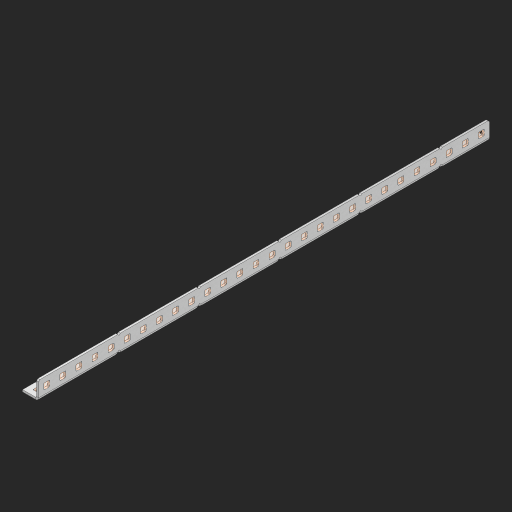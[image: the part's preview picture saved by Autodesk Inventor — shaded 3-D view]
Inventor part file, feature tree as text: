
AUTODESK INVENTOR PART (.ipt)
format: ipt  version: 2023 (Build 270158000, 158)  size: 1,191,936 bytes
history: native  units: in
note: dims shown in document units (in); Inventor stores cm internally (conversion verified against a paired STEP export)
features: other x232, extrude x82, sheet_metal_op x11, sketch x10, pattern_linear x2, mirror x1, chamfer x1
ambient origin geometry x8: Origin, YZ Plane, XZ Plane, XY Plane, X Axis, Y Axis, Z Axis, Center Point
bodies: Solid1 (feature_tree), Body (feature_tree)
feature tree (339):
  other  "Alu Half C 1x2x1x28"
  other  "Table"
  other  "Alu C 1x2x1x35"
  other  "Alu C 1x2x1x34"
  other  "Alu C 1x2x1x33"
  other  "Alu C 1x2x1x32"
  other  "Alu C 1x2x1x31"
  other  "Alu C 1x2x1x30"
  other  "Alu C 1x2x1x29"
  other  "Alu C 1x2x1x28"
  other  "Alu C 1x2x1x27"
  other  "Alu C 1x2x1x26"
  other  "Alu C 1x2x1x25"
  other  "Alu C 1x2x1x24"
  other  "Alu C 1x2x1x23"
  other  "Alu C 1x2x1x22"
  other  "Alu C 1x2x1x21"
  other  "Alu C 1x2x1x20"
  other  "Alu C 1x2x1x19"
  other  "Alu C 1x2x1x18"
  other  "Alu C 1x2x1x17"
  other  "Alu C 1x2x1x16"
  other  "Alu C 1x2x1x15"
  other  "Alu C 1x2x1x14"
  other  "Alu C 1x2x1x13"
  other  "Alu C 1x2x1x12"
  other  "Alu C 1x2x1x11"
  other  "Alu C 1x2x1x10"
  other  "Alu C 1x2x1x9"
  other  "Alu C 1x2x1x8"
  other  "Alu C 1x2x1x7"
  other  "Alu C 1x2x1x6"
  other  "Alu C 1x2x1x5"
  other  "Alu C 1x2x1x4"
  other  "Alu C 1x2x1x3"
  other  "Alu C 1x2x1x2"
  other  "Alu C 1x2x1x1"
  other  "Steel C 1x2x1x35"
  other  "Steel C 1x2x1x34"
  other  "Steel C 1x2x1x33"
  other  "Steel C 1x2x1x32"
  other  "Steel C 1x2x1x31"
  other  "Steel C 1x2x1x30"
  other  "Steel C 1x2x1x29"
  other  "Steel C 1x2x1x28"
  other  "Steel C 1x2x1x27"
  other  "Steel C 1x2x1x26"
  other  "Steel C 1x2x1x25"
  other  "Steel C 1x2x1x24"
  other  "Steel C 1x2x1x23"
  other  "Steel C 1x2x1x22"
  other  "Steel C 1x2x1x21"
  other  "Steel C 1x2x1x20"
  other  "Steel C 1x2x1x19"
  other  "Steel C 1x2x1x18"
  other  "Steel C 1x2x1x17"
  other  "Steel C 1x2x1x16"
  other  "Steel C 1x2x1x15"
  other  "Steel C 1x2x1x14"
  other  "Steel C 1x2x1x13"
  other  "Steel C 1x2x1x12"
  other  "Steel C 1x2x1x11"
  other  "Steel C 1x2x1x10"
  other  "Steel C 1x2x1x9"
  other  "Steel C 1x2x1x8"
  other  "Steel C 1x2x1x7"
  other  "Steel C 1x2x1x6"
  other  "Steel C 1x2x1x5"
  other  "Steel C 1x2x1x4"
  other  "Steel C 1x2x1x3"
  other  "Steel C 1x2x1x2"
  other  "Steel C 1x2x1x1"
  other  "Alu Half C 1x2x1x35"
  other  "Alu Half C 1x2x1x34"
  other  "Alu Half C 1x2x1x33"
  other  "Alu Half C 1x2x1x32"
  other  "Alu Half C 1x2x1x31"
  other  "Alu Half C 1x2x1x30"
  other  "Alu Half C 1x2x1x29"
  other  "Alu Half C 1x2x1x27"
  other  "Alu Half C 1x2x1x26"
  other  "Alu Half C 1x2x1x25"
  other  "Alu Half C 1x2x1x24"
  other  "Alu Half C 1x2x1x23"
  other  "Alu Half C 1x2x1x22"
  other  "Alu Half C 1x2x1x21"
  other  "Alu Half C 1x2x1x20"
  other  "Alu Half C 1x2x1x19"
  other  "Alu Half C 1x2x1x18"
  other  "Alu Half C 1x2x1x17"
  other  "Alu Half C 1x2x1x16"
  other  "Alu Half C 1x2x1x15"
  other  "Alu Half C 1x2x1x14"
  other  "Alu Half C 1x2x1x13"
  other  "Alu Half C 1x2x1x12"
  other  "Alu Half C 1x2x1x11"
  other  "Alu Half C 1x2x1x10"
  other  "Alu Half C 1x2x1x9"
  other  "Alu Half C 1x2x1x8"
  other  "Alu Half C 1x2x1x7"
  other  "Alu Half C 1x2x1x6"
  other  "Alu Half C 1x2x1x5"
  other  "Alu Half C 1x2x1x4"
  other  "Alu Half C 1x2x1x3"
  other  "Alu Half C 1x2x1x2"
  other  "Alu Half C 1x2x1x1"
  other  "Steel Half C 1x2x1x35"
  other  "Steel Half C 1x2x1x34"
  other  "Steel Half C 1x2x1x33"
  other  "Steel Half C 1x2x1x32"
  other  "Steel Half C 1x2x1x31"
  other  "Steel Half C 1x2x1x30"
  other  "Steel Half C 1x2x1x29"
  other  "Steel Half C 1x2x1x28"
  other  "Steel Half C 1x2x1x27"
  other  "Steel Half C 1x2x1x26"
  other  "Steel Half C 1x2x1x25"
  other  "Steel Half C 1x2x1x24"
  other  "Steel Half C 1x2x1x23"
  other  "Steel Half C 1x2x1x22"
  other  "Steel Half C 1x2x1x21"
  other  "Steel Half C 1x2x1x20"
  other  "Steel Half C 1x2x1x19"
  other  "Steel Half C 1x2x1x18"
  other  "Steel Half C 1x2x1x17"
  other  "Steel Half C 1x2x1x16"
  other  "Steel Half C 1x2x1x15"
  other  "Steel Half C 1x2x1x14"
  other  "Steel Half C 1x2x1x13"
  other  "Steel Half C 1x2x1x12"
  other  "Steel Half C 1x2x1x11"
  other  "Steel Half C 1x2x1x10"
  other  "Steel Half C 1x2x1x9"
  other  "Steel Half C 1x2x1x8"
  other  "Steel Half C 1x2x1x7"
  other  "Steel Half C 1x2x1x6"
  other  "Steel Half C 1x2x1x5"
  other  "Steel Half C 1x2x1x4"
  other  "Steel Half C 1x2x1x3"
  other  "Steel Half C 1x2x1x2"
  other  "Steel Half C 1x2x1x1"
  sheet_metal_op  "Flanges"
  other  "Flange Pattern Plane"
  other  "Flange Pattern Sketch"
  sheet_metal_op  "Flange Pattern"
  sheet_metal_op  "Body Pattern"
  pattern_linear  "Center Pattern"  Spacing1=0.0625in  [1 undecoded]
  other  "Arc Length"
  mirror  "Notch Mirror"
  pattern_linear  "Notch Pattern"  Spacing1=0.182in  [1 undecoded]
  chamfer  "End Chamfer"
  extrude  "Half Cut"  Depth=0.02in
  sketch  "Sketch1"  dims[d0=1.0in]
  other  "Plate1"
  sketch  "Sketch2"  dims[d1=14.0in]
  other  "Plate2"
  sheet_metal_op  "Bend1"
  sheet_metal_op  "Corner1"
  sketch  "Sketch3"  dims[d2=0.0625in]
  sketch  "Sketch7"  dims[d3=0.0625in]
  other  "Srf1"
  other  "Srf2"
  sketch  "Sketch8"  dims[d4=0.0312in]
  sketch  "Sketch9"  dims[d5=0.125in]
  other  "Srf91"
  sheet_metal_op  "Body Pattern Sketch"
  other  "Srf92"
  sketch  "Sketch13"  dims[d6=0.0625in]
  sketch  "Sketch14"  dims[d7=0.5in d8=90.0deg d9=0.0312in]
  sketch  "Sketch15"  dims[d10=0.25in]
  sketch  "Sketch16"  dims[d11=0.0625in d12=0.0625in d16=0.182in d17=0.02in d18=0.0625in d19=0.0in d20=0.25in d21=0.25in d38=11.0236in d40=0.5in d41=0.3937in d43=1.0in d46=0.172in d47=1.0in d48=0.0in d49=0.182in d50=0.02in d51=0.25in d52=0.25in d53=0.0625in d54=0.0in d55=0.172in d56=1.0in d57=0.0in d58=0.25in d60=11.0236in d62=0.5in d63=0.3937in d65=0.5in d85=0.1473in d86=0.1782in d88=0.04in d89=0.0625in d90=0.0in d91=0.04in d92=0.0491in d95=2.5in d96=0.04in d97=0.25in d98=45.0deg d99=0.25in d100=0.5in d101=0.0in d102=2.497in d106=0.182in d107=0.02in d108=0.5in d109=0.5in d110=0.0625in d111=0.0in d112=0.172in d113=0.5in d114=0.0in d117=0.5in d118=0.5in d119=0.5in]
  other  "Srf786"
  other  "Srf823"
  other  "Srf824"
  other  "Srf825"
  other  "Srf826"
  other  "Srf827"
  other  "Srf828"
  other  "Srf829"
  other  "Srf856"
  other  "Srf857"
  other  "Srf858"
  other  "Srf859"
  other  "Srf860"
  other  "Srf861"
  other  "Srf862"
  other  "Srf889"
  other  "Srf890"
  other  "Srf891"
  other  "Srf892"
  other  "Srf893"
  other  "Srf894"
  other  "Srf895"
  other  "Srf896"
  other  "Srf922"
  other  "Srf923"
  other  "Srf924"
  other  "Srf925"
  other  "Srf926"
  other  "Srf959"
  other  "Srf960"
  other  "Srf961"
  other  "Srf962"
  other  "Srf963"
  other  "Srf996"
  other  "Srf997"
  other  "Srf998"
  other  "Srf999"
  other  "Srf1000"
  other  "Srf1143"
  other  "Srf1144"
  other  "Srf1145"
  other  "Srf1146"
  other  "Srf1147"
  other  "Srf1148"
  other  "Srf1149"
  other  "Srf1150"
  other  "Srf1151"
  other  "Srf1152"
  other  "Srf1153"
  other  "Srf1154"
  other  "Srf1155"
  other  "Srf1156"
  other  "Srf1199"
  other  "Srf1200"
  other  "Srf1201"
  other  "Srf1202"
  other  "Srf1203"
  other  "Srf1204"
  other  "Srf1205"
  other  "Srf1206"
  other  "Srf1207"
  other  "Srf1208"
  other  "Srf1209"
  other  "Srf1210"
  other  "Srf1211"
  other  "Srf1212"
  other  "Srf1255"
  other  "Srf1256"
  other  "Srf1257"
  other  "Srf1258"
  other  "Srf1259"
  other  "Srf1260"
  other  "Srf1261"
  other  "Srf1262"
  other  "Srf1263"
  other  "Srf1264"
  other  "Srf1265"
  other  "Srf1266"
  other  "Srf1267"
  other  "Srf1268"
  sheet_metal_op  "Flange Stamp"
  sheet_metal_op  "Flange Circle"
  sheet_metal_op  "Body Stamp"
  sheet_metal_op  "Body Circle"
  other  "Center Stamp"
  other  "Center Circle"
  sheet_metal_op  "Notch"
  extrude  "ExtrusionSrf2"  Depth=0.0625in
  extrude  "ExtrusionSrf92"  TaperAngle=0.0deg  [1 undecoded]
  extrude  "ExtrusionSrf823"  Depth=0.25in
  extrude  "ExtrusionSrf824"  Depth=0.25in
  extrude  "ExtrusionSrf825"  Depth=0.5in
  extrude  "ExtrusionSrf826"  Depth=0.5in
  extrude  "ExtrusionSrf827"  Depth=1.0in TaperAngle=0.0deg
  extrude  "ExtrusionSrf828"  Depth=0.182in
  extrude  "ExtrusionSrf829"  Depth=0.02in
  extrude  "ExtrusionSrf856"  Depth=0.25in
  extrude  "ExtrusionSrf857"  Depth=0.25in
  extrude  "ExtrusionSrf858"  Depth=0.0625in
  extrude  "ExtrusionSrf859"  TaperAngle=0.0deg  [1 undecoded]
  extrude  "ExtrusionSrf860"  Depth=0.5in
  extrude  "ExtrusionSrf861"  Depth=1.0in TaperAngle=0.0deg
  extrude  "ExtrusionSrf862"  Depth=0.25in
  extrude  "ExtrusionSrf889"  Depth=0.5in
  extrude  "ExtrusionSrf890"  Depth=0.5in
  extrude  "ExtrusionSrf891"  Depth=0.5in
  extrude  "ExtrusionSrf892"  Depth=0.5in
  extrude  "ExtrusionSrf893"  Depth=0.5in
  extrude  "ExtrusionSrf894"  Depth=0.0625in
  extrude  "ExtrusionSrf895"  TaperAngle=0.0deg  [1 undecoded]
  extrude  "ExtrusionSrf896"  Depth=0.5in
  extrude  "ExtrusionSrf922"  Depth=0.5in
  extrude  "ExtrusionSrf923"  Depth=2.5in
  extrude  "ExtrusionSrf924"  Depth=0.25in TaperAngle=45.0deg
  extrude  "ExtrusionSrf925"  Depth=0.25in
  extrude  "ExtrusionSrf926"  Depth=0.5in TaperAngle=0.0deg
  extrude  "ExtrusionSrf959"  Depth=0.5in
  extrude  "ExtrusionSrf960"  Depth=0.182in
  extrude  "ExtrusionSrf961"  Depth=0.02in
  extrude  "ExtrusionSrf962"  Depth=0.5in
  extrude  "ExtrusionSrf963"  Depth=0.5in
  extrude  "ExtrusionSrf996"  Depth=0.0625in
  extrude  "ExtrusionSrf997"  TaperAngle=0.0deg  [1 undecoded]
  extrude  "ExtrusionSrf998"  Depth=0.5in
  extrude  "ExtrusionSrf999"  Depth=0.5in TaperAngle=0.0deg
  extrude  "ExtrusionSrf1000"  Depth=0.5in
  extrude  "ExtrusionSrf1143"  Depth=0.5in
  extrude  "ExtrusionSrf1144"  Depth=0.5in
  extrude  "ExtrusionSrf1145"  [1 undecoded]
  extrude  "ExtrusionSrf1146"  [1 undecoded]
  extrude  "ExtrusionSrf1147"  [1 undecoded]
  extrude  "ExtrusionSrf1148"  [1 undecoded]
  extrude  "ExtrusionSrf1149"  [1 undecoded]
  extrude  "ExtrusionSrf1150"  [1 undecoded]
  extrude  "ExtrusionSrf1151"  [1 undecoded]
  extrude  "ExtrusionSrf1152"  [1 undecoded]
  extrude  "ExtrusionSrf1153"  [1 undecoded]
  extrude  "ExtrusionSrf1154"  [1 undecoded]
  extrude  "ExtrusionSrf1155"  [1 undecoded]
  extrude  "ExtrusionSrf1156"  [1 undecoded]
  extrude  "ExtrusionSrf1199"  [1 undecoded]
  extrude  "ExtrusionSrf1200"  [1 undecoded]
  extrude  "ExtrusionSrf1201"  [1 undecoded]
  extrude  "ExtrusionSrf1202"  [1 undecoded]
  extrude  "ExtrusionSrf1203"  [1 undecoded]
  extrude  "ExtrusionSrf1204"  [1 undecoded]
  extrude  "ExtrusionSrf1205"  [1 undecoded]
  extrude  "ExtrusionSrf1206"  [1 undecoded]
  extrude  "ExtrusionSrf1207"  [1 undecoded]
  extrude  "ExtrusionSrf1208"  [1 undecoded]
  extrude  "ExtrusionSrf1209"  [1 undecoded]
  extrude  "ExtrusionSrf1210"  [1 undecoded]
  extrude  "ExtrusionSrf1211"  [1 undecoded]
  extrude  "ExtrusionSrf1212"  [1 undecoded]
  extrude  "ExtrusionSrf1255"  [1 undecoded]
  extrude  "ExtrusionSrf1256"  [1 undecoded]
  extrude  "ExtrusionSrf1257"  [1 undecoded]
  extrude  "ExtrusionSrf1258"  [1 undecoded]
  extrude  "ExtrusionSrf1259"  [1 undecoded]
  extrude  "ExtrusionSrf1260"  [1 undecoded]
  extrude  "ExtrusionSrf1261"  [1 undecoded]
  extrude  "ExtrusionSrf1262"  [1 undecoded]
  extrude  "ExtrusionSrf1263"  [1 undecoded]
  extrude  "ExtrusionSrf1264"  [1 undecoded]
  extrude  "ExtrusionSrf1265"  [1 undecoded]
  extrude  "ExtrusionSrf1266"  [1 undecoded]
  extrude  "ExtrusionSrf1267"  [1 undecoded]
  extrude  "ExtrusionSrf1268"  [1 undecoded]
note: 46 required parameter values undecoded (feature->parameter linkage not recoverable at this tier; creation-order binding heuristic only, values carry confidence <= 0.55)
